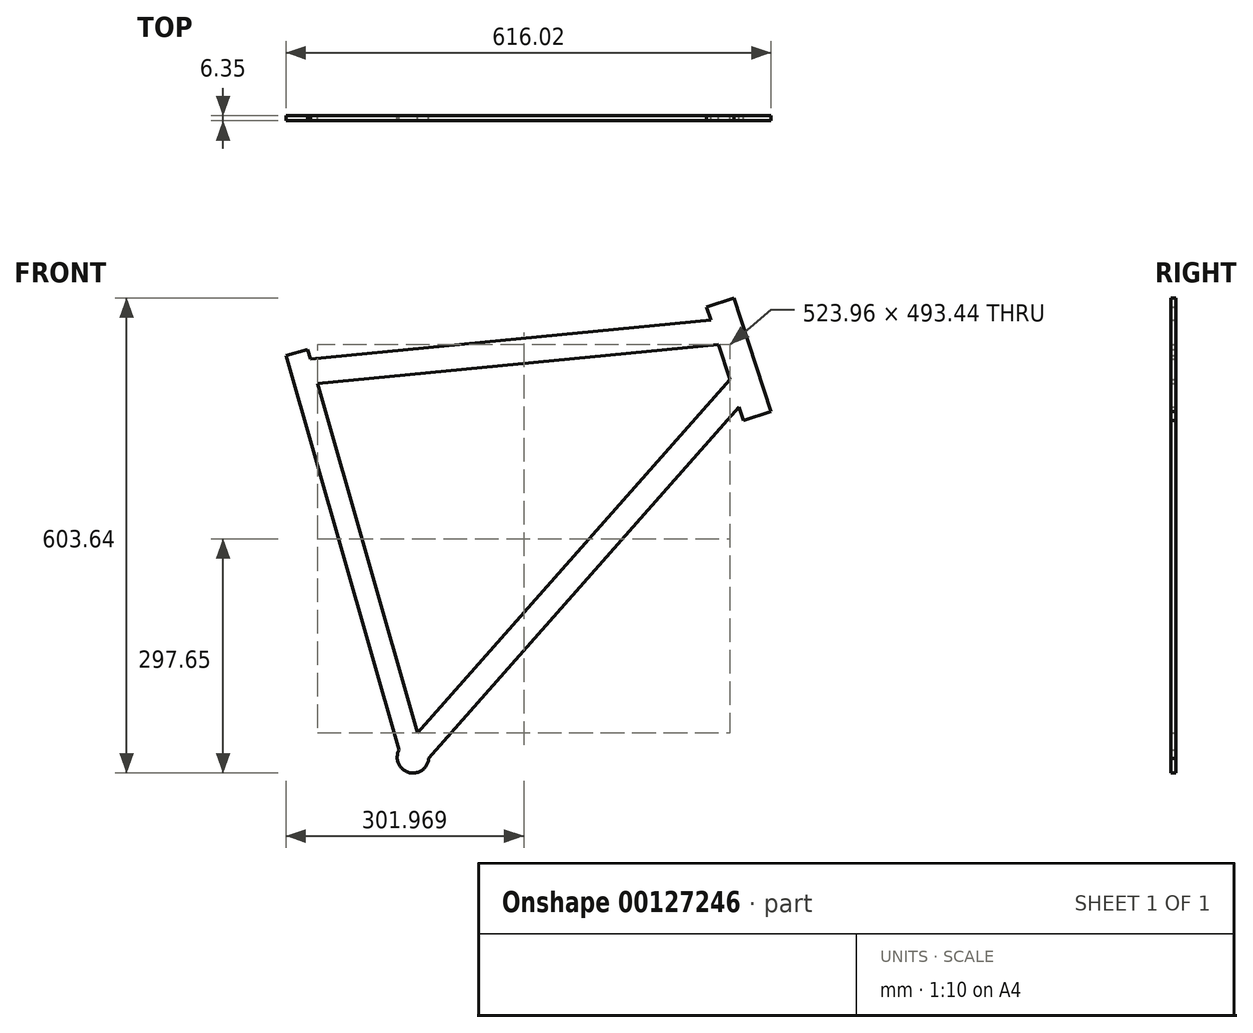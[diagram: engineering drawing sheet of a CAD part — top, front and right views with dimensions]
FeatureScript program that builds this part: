
annotation { "Feature Type Name" : "Feature", "Feature Type Description" : "" }
export const myFeature = defineFeature(function(context is Context, id is Id, definition is map)
    precondition{}
    {
        {
            var Q0;
            Q0=qCreatedBy(makeId("Front.planeOp"),FACE);
            var sketch = newSketch(context, id + "F0", { "sketchPlane" : qUnion([Q0])});
            skLineSegment(sketch, "E0", {"start": v(0, 0) * mm, "end": v(-128.45, 447.95) * mm, "construction": true});
            skLineSegment(sketch, "E1", {"start": v(437.17, 433.61) * mm, "end": v(390.3, 577.85) * mm, "construction": true});
            skLineSegment(sketch, "E2", {"start": v(0, 0) * mm, "end": v(-435.89, 60) * mm});
            skLineSegment(sketch, "E3", {"start": v(-783.58, -276) * mm, "end": v(815.72, -276) * mm, "construction": true});
            skLineSegment(sketch, "E4", {"start": v(-128.45, 447.95) * mm, "end": v(-147.47, 514.28) * mm, "construction": true});
            skLineSegment(sketch, "E5", {"start": v(390.3, 577.85) * mm, "end": v(-165.7, 577.85) * mm, "construction": true});
            skLineSegment(sketch, "E6", {"start": v(419.58, 427.9) * mm, "end": v(454.76, 439.33) * mm});
            skLineSegment(sketch, "E7", {"start": v(454.76, 439.33) * mm, "end": v(407.9, 583.57) * mm});
            skLineSegment(sketch, "E8", {"start": v(407.9, 583.57) * mm, "end": v(372.7, 572.13) * mm});
            skLineSegment(sketch, "E9", {"start": v(372.7, 572.13) * mm, "end": v(419.58, 427.9) * mm});
            skCircle(sketch, "E10", {"center": v(0, 0) * mm, "radius": 20.07 * mm});
            skLineSegment(sketch, "E11", {"start": v(9.93, 17.44) * mm, "end": v(-133.67, 518.23) * mm});
            skLineSegment(sketch, "E12", {"start": v(-133.67, 518.23) * mm, "end": v(-161.26, 510.32) * mm});
            skLineSegment(sketch, "E13", {"start": v(-161.26, 510.32) * mm, "end": v(-17.66, 9.53) * mm});
            skLineSegment(sketch, "E14", {"start": v(-435.89, 60) * mm, "end": v(-143.34, 447.84) * mm});
            skLineSegment(sketch, "E15", {"start": v(0, 0) * mm, "end": v(408.38, 462.34) * mm, "construction": true});
            skLineSegment(sketch, "E16", {"start": v(6.08, 30.86) * mm, "end": v(402.69, 479.87) * mm});
            skLineSegment(sketch, "E17", {"start": v(402.69, 479.87) * mm, "end": v(414.08, 444.8) * mm, "construction": true});
            skLineSegment(sketch, "E18", {"start": v(414.08, 444.8) * mm, "end": v(20.02, -1.31) * mm});
            skLineSegment(sketch, "E19", {"start": v(-125.72, 490.5) * mm, "end": v(383.23, 539.76) * mm, "construction": true});
            skLineSegment(sketch, "E20", {"start": v(-121.27, 474.99) * mm, "end": v(-130.17, 506.02) * mm, "construction": true});
            skLineSegment(sketch, "E21", {"start": v(-130.17, 506.02) * mm, "end": v(378.2, 555.22) * mm});
            skLineSegment(sketch, "E22", {"start": v(378.2, 555.22) * mm, "end": v(388.25, 524.3) * mm, "construction": true});
            skLineSegment(sketch, "E23", {"start": v(388.25, 524.3) * mm, "end": v(-121.27, 474.99) * mm});
            skLineSegment(sketch, "E24", {"start": v(6.08, 30.86) * mm, "end": v(17.98, 20.35) * mm, "construction": true});
            skLineSegment(sketch, "E25", {"start": v(17.98, 20.35) * mm, "end": v(29.88, 9.84) * mm, "construction": true});
            skLineSegment(sketch, "E26", {"start": v(-435.89, 60) * mm, "end": v(689.89, 60) * mm, "construction": true});
            skLineSegment(sketch, "E27", {"start": v(437.17, 433.61) * mm, "end": v(440.26, 424.1) * mm, "construction": true});
            skLineSegment(sketch, "E28", {"start": v(440.26, 424.1) * mm, "end": v(563.08, 46.1) * mm});
            skLineSegment(sketch, "E29", {"start": v(563.08, 46.1) * mm, "end": v(605.88, 60) * mm});
            skCircle(sketch, "E30", {"center": v(605.88, 60) * mm, "radius": 336 * mm});
            skCircle(sketch, "E31", {"center": v(-435.89, 60) * mm, "radius": 336 * mm});
            skLineSegment(sketch, "E32", {"start": v(0, 0) * mm, "end": v(170, 0) * mm, "construction": true});
            skPoint(sketch, "E33", {"position": v(-5.53, 19.29) * mm});
            skPoint(sketch, "E34", {"position": v(13.28, 15.04) * mm});
            skSolve(sketch);
        }
        {
            var Q0;
            {var subQ3=sQuery(id+"F0.wireOp",EDGE,"E6");Q0=makeQuery(id+"F0.imprint","IMPRINT",FACE,{"disambiguationData":[TD([[makeQuery(id+"F0.imprint","IMPRINT",EDGE,{"derivedFrom":subQ3}),1.0]])]});}
            var Q1;
            {var subQ0=sQuery(id+"F0.wireOp",EDGE,"E21");Q1=makeQuery(id+"F0.imprint","IMPRINT",FACE,{"disambiguationData":[TD([[makeQuery(id+"F0.imprint","IMPRINT",EDGE,{"derivedFrom":subQ0}),-1.0]])]});}
            var Q2;
            {var subQ0=sQuery(id+"F0.wireOp",EDGE,"E10");var subQ1=makeQuery(id+"F0.imprint","INTERSECT",VERTEX,{"derivedFrom":[subQ0,sQuery(id+"F0.wireOp",EDGE,"E11")]});Q2=makeQuery(id+"F0.imprint","IMPRINT",FACE,{"disambiguationData":[TD([[makeQuery(id+"F0.imprint","IMPRINT",EDGE,{"disambiguationData":[TD([[subQ1,-1.0]])],"derivedFrom":subQ0}),1.0]])]});}
            var Q3;
            {var subQ0=sQuery(id+"F0.wireOp",EDGE,"E16");Q3=makeQuery(id+"F0.imprint","IMPRINT",FACE,{"disambiguationData":[TD([[makeQuery(id+"F0.imprint","IMPRINT",EDGE,{"derivedFrom":subQ0}),-1.0]])]});}
            var Q4;
            {var subQ6=sQuery(id+"F0.wireOp",EDGE,"E12");Q4=makeQuery(id+"F0.imprint","IMPRINT",FACE,{"disambiguationData":[TD([[makeQuery(id+"F0.imprint","IMPRINT",EDGE,{"derivedFrom":subQ6}),1.0]])]});}
            extrude(context, id + "F1", {"entities" : qUnion([Q0, Q1, Q2, Q3, Q4]), "depth" : 6.35 * mm});
        }
    });
